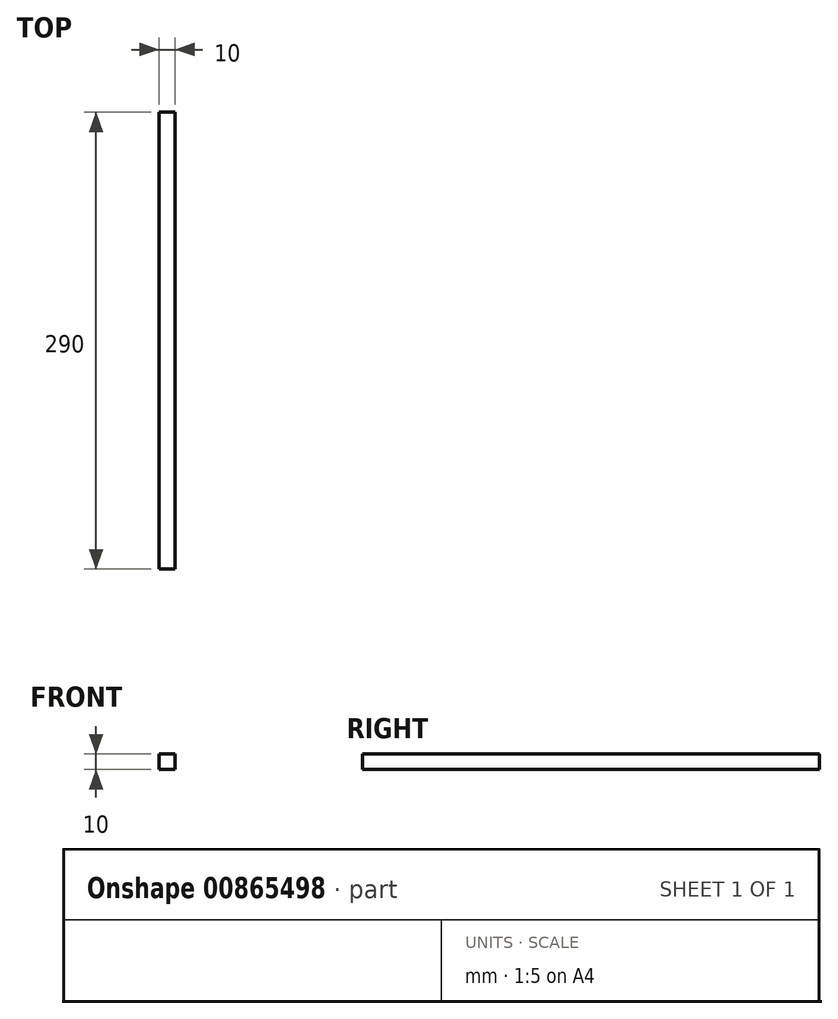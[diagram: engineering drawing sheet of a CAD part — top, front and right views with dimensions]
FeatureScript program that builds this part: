
annotation { "Feature Type Name" : "Feature", "Feature Type Description" : "" }
export const myFeature = defineFeature(function(context is Context, id is Id, definition is map)
    precondition{}
    {
        {
            var Q0;
            Q0=qCreatedBy(makeId("Front.planeOp"),FACE);
            var sketch = newSketch(context, id + "F0", { "sketchPlane" : qUnion([Q0])});
            skLineSegment(sketch, "E0", {"start": v(0, 0) * mm, "end": v(0, -10) * mm});
            skLineSegment(sketch, "E1", {"start": v(0, -10) * mm, "end": v(10, -10) * mm});
            skLineSegment(sketch, "E2", {"start": v(10, -10) * mm, "end": v(10, 0) * mm});
            skLineSegment(sketch, "E3", {"start": v(10, 0) * mm, "end": v(0, 0) * mm});
            skSolve(sketch);
        }
        {
            var Q0;
            Q0=makeQuery(id+"F0.imprint","IMPRINT",FACE,{"disambiguationData":[TD([[makeQuery(id+"F0.imprint","IMPRINT",EDGE,{"derivedFrom":sQuery(id+"F0.wireOp",EDGE,"E0")}),1.0]])]});
            extrude(context, id + "F1", {"entities" : qUnion([Q0]), "endBound" : BoundingType.SYMMETRIC, "depth" : 290 * mm, "offsetDistance" : 25 * mm});
        }
    });
